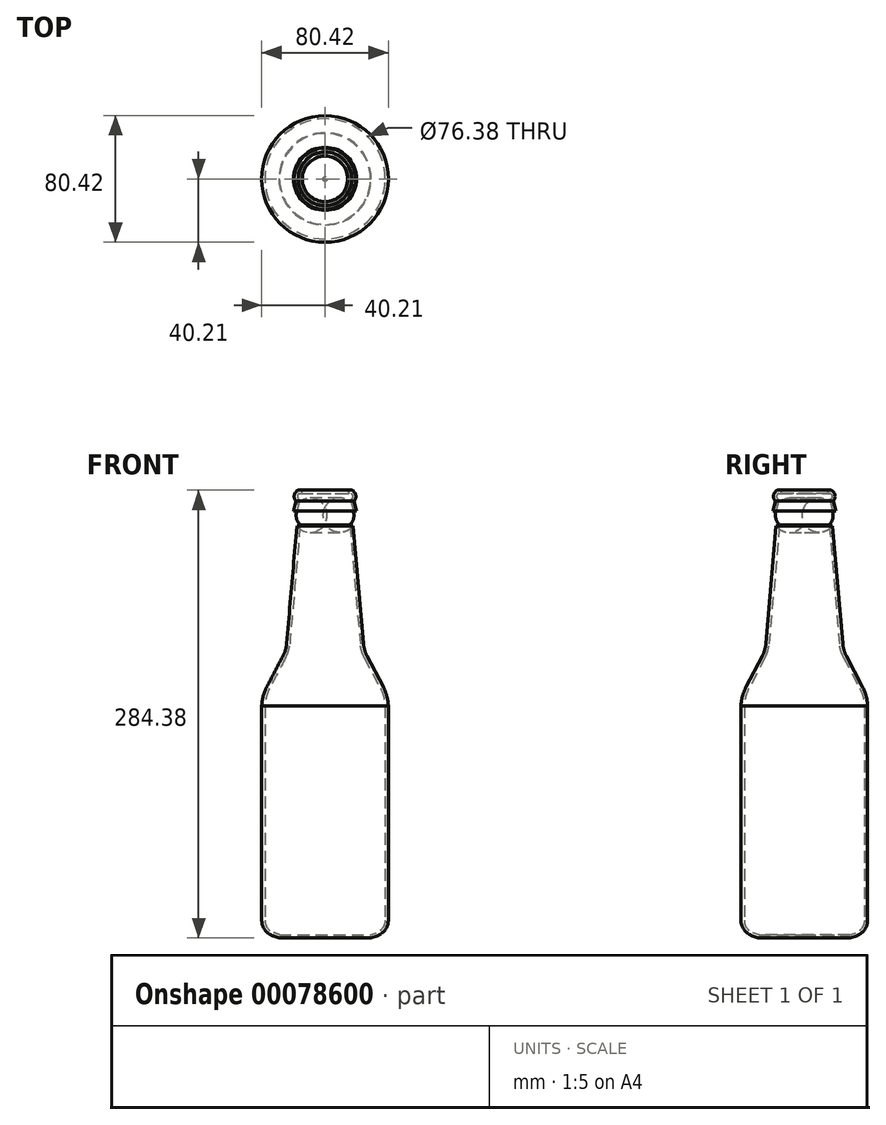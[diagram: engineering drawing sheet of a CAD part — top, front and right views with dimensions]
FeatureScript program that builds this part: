
annotation { "Feature Type Name" : "Feature", "Feature Type Description" : "" }
export const myFeature = defineFeature(function(context is Context, id is Id, definition is map)
    precondition{}
    {
        {
            var Q0;
            Q0=qCreatedBy(makeId("Front.planeOp"),FACE);
            var sketch = newSketch(context, id + "F0", { "sketchPlane" : qUnion([Q0])});
            skLineSegment(sketch, "E0", {"start": v(0, -52.78) * mm, "end": v(0, 318.91) * mm, "construction": true});
            skLineSegment(sketch, "E1", {"start": v(17.88, 272.92) * mm, "end": v(24.4, 198.33) * mm});
            skArc(sketch, "E2", {"start": v(17.88, 272.92) * mm, "mid": v(20.08, 277.4) * mm, "end": v(20.05, 282.4) * mm});
            skLineSegment(sketch, "E3", {"start": v(20.05, 282.4) * mm, "end": v(18.49, 288.83) * mm});
            skArc(sketch, "E4", {"start": v(18.49, 288.83) * mm, "mid": v(19.5, 292.67) * mm, "end": v(17.04, 295.77) * mm});
            skArc(sketch, "E5", {"start": v(24.4, 198.33) * mm, "mid": v(25.15, 194.35) * mm, "end": v(26.66, 190.59) * mm});
            skLineSegment(sketch, "E6", {"start": v(26.66, 190.59) * mm, "end": v(37, 170.75) * mm});
            skArc(sketch, "E7", {"start": v(40.21, 158.65) * mm, "mid": v(39.28, 164.88) * mm, "end": v(37, 170.75) * mm});
            skLineSegment(sketch, "E8", {"start": v(40.21, 158.65) * mm, "end": v(40.21, 98.32) * mm});
            skLineSegment(sketch, "E9", {"start": v(40.21, 98.32) * mm, "end": v(40.21, 22.6) * mm});
            skArc(sketch, "E10", {"start": v(33.34, 12.83) * mm, "mid": v(38.32, 16.63) * mm, "end": v(40.21, 22.6) * mm});
            skLineSegment(sketch, "E11", {"start": v(33.34, 12.83) * mm, "end": v(29.31, 11.39) * mm});
            skLineSegment(sketch, "E12", {"start": v(29.31, 11.39) * mm, "end": v(0, 11.39) * mm});
            skLineSegment(sketch, "E13.0", {"start": v(28.96, 13.41) * mm, "end": v(0, 13.41) * mm});
            skLineSegment(sketch, "E13.1", {"start": v(32.66, 14.74) * mm, "end": v(28.96, 13.41) * mm});
            skArc(sketch, "E13.2", {"start": v(32.66, 14.74) * mm, "mid": v(36.67, 17.8) * mm, "end": v(38.19, 22.6) * mm});
            skArc(sketch, "E13.3", {"start": v(15.78, 273.62) * mm, "mid": v(18, 277.47) * mm, "end": v(18.08, 281.93) * mm});
            skLineSegment(sketch, "E13.4", {"start": v(18.08, 281.93) * mm, "end": v(16.22, 289.6) * mm});
            skArc(sketch, "E13.5", {"start": v(16.22, 289.6) * mm, "mid": v(17.56, 291.59) * mm, "end": v(16.52, 293.75) * mm});
            skLineSegment(sketch, "E13.7", {"start": v(15.78, 273.62) * mm, "end": v(22.39, 198.16) * mm});
            skArc(sketch, "E13.8", {"start": v(22.39, 198.16) * mm, "mid": v(23.2, 193.78) * mm, "end": v(24.87, 189.65) * mm});
            skLineSegment(sketch, "E13.9", {"start": v(24.87, 189.65) * mm, "end": v(35.2, 169.82) * mm});
            skArc(sketch, "E13.10", {"start": v(38.19, 158.6) * mm, "mid": v(37.31, 164.38) * mm, "end": v(35.2, 169.82) * mm});
            skLineSegment(sketch, "E13.11", {"start": v(38.19, 158.6) * mm, "end": v(38.19, 98.32) * mm});
            skLineSegment(sketch, "E13.12", {"start": v(38.19, 98.32) * mm, "end": v(38.19, 22.6) * mm});
            skLineSegment(sketch, "E14", {"start": v(0, 13.41) * mm, "end": v(0, 11.39) * mm});
            skLineSegment(sketch, "E15", {"start": v(14.42, 295.77) * mm, "end": v(15.16, 293.75) * mm});
            skLineSegment(sketch, "E16", {"start": v(14.42, 295.77) * mm, "end": v(17.04, 295.77) * mm});
            skLineSegment(sketch, "E17", {"start": v(15.16, 293.75) * mm, "end": v(16.52, 293.75) * mm});
            skSolve(sketch);
        }
        {
            var Q0;
            Q0 = qSketchRegion(id + "F0", true);
            var Q1;
            Q1=sQuery(id+"F0.wireOp",EDGE,"E0");
            revolve(context, id + "F1", {"entities" : qUnion([Q0]), "axis" : qUnion([Q1]), "revolveType" : RevolveType.FULL});
        }
    });
